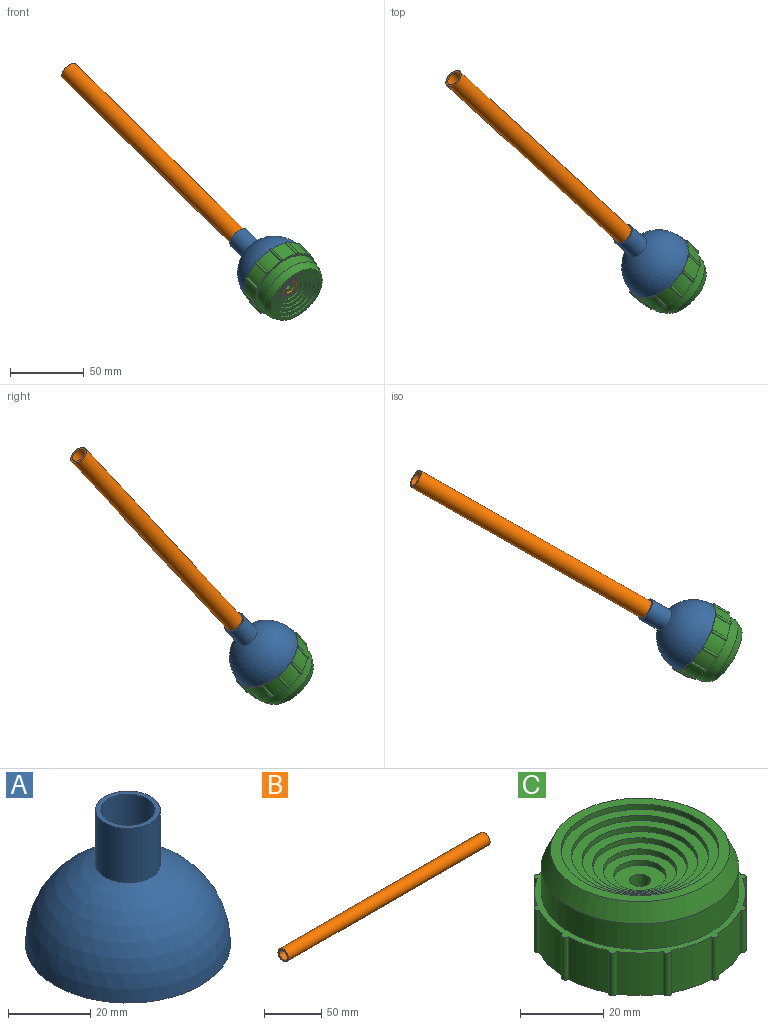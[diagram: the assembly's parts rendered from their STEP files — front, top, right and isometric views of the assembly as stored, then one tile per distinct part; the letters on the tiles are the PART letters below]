
ASSEMBLY  parts=3 mates=4
PART A: 5 faces, bbox 50x50x40 mm
  f0: cylinder r=7.87mm len=16.27mm, axis (0,0,-1), area 805.1mm2, adj f1,f3
  f1: sphere r=25mm, area 3727.1mm2, adj f0,f2
  f2: plane 50x50mm, normal (0,0,-1), area 1826.5mm2, adj f1,f4
  f3: plane 15.75x15.75mm, normal (0,0,1), area 57.8mm2, adj f0,f4
  f4: cylinder r=6.6mm len=40mm, axis (0,0,1), area 1659.8mm2, adj f2,f3
PART B: 4 faces, bbox 250x13x13 mm
  f0: cylinder r=4.92mm len=250mm, axis (-1,0,0), area 7733.1mm2, adj f2,f3
  f1: cylinder r=6.48mm len=250mm, axis (-1,0,0), area 10174mm2, adj f2,f3
  f2: plane 12.95x12.95mm, normal (1,0,0), area 55.7mm2, adj f0,f1
  f3: plane 12.95x12.95mm, normal (-1,0,0), area 55.7mm2, adj f0,f1
PART C: 44 faces, bbox 52.8x52.8x25 mm
  f0: cylinder r=25.4mm len=12.5mm, axis (0,0,1), area 141.2mm2, adj f27,f28,f29,f40
  f1: cylinder r=25.4mm len=12.5mm, axis (0,0,1), area 141.2mm2, adj f27,f28,f39,f40
  f2: cylinder r=25.4mm len=12.5mm, axis (0,0,1), area 141.2mm2, adj f27,f28,f38,f39
  f3: cylinder r=25.4mm len=12.5mm, axis (0,0,1), area 141.2mm2, adj f27,f28,f37,f38
  f4: cylinder r=25.4mm len=12.5mm, axis (0,0,1), area 141.2mm2, adj f27,f28,f36,f37
  f5: cylinder r=25.4mm len=12.5mm, axis (0,0,1), area 141.2mm2, adj f27,f28,f35,f36
  f6: cylinder r=25.4mm len=12.5mm, axis (0,0,1), area 141.2mm2, adj f27,f28,f34,f35
  f7: cylinder r=25.4mm len=12.5mm, axis (0,0,1), area 141.2mm2, adj f27,f28,f33,f34
  f8: cylinder r=25.4mm len=12.5mm, axis (0,0,1), area 141.2mm2, adj f27,f28,f32,f33
  f9: cylinder r=25.4mm len=12.5mm, axis (0,0,1), area 141.2mm2, adj f27,f28,f31,f32
  f10: cylinder r=25.4mm len=12.5mm, axis (0,0,1), area 141.2mm2, adj f27,f28,f30,f31
  f11: cylinder r=25.4mm len=12.5mm, axis (0,0,1), area 141.2mm2, adj f27,f28,f29,f30
  f12: plane 12.7x12.7mm, normal (0,0,1), area 106.4mm2, adj f13,f43
  f13: cylinder r=6.35mm len=12.7mm, axis (0,0,1), area 59.8mm2, adj f12,f14
  f14: plane 17.78x17.78mm, normal (0,0,1), area 121.6mm2, adj f13,f15
  f15: cylinder r=8.89mm len=17.78mm, axis (0,0,1), area 83.8mm2, adj f14,f16
  f16: plane 22.86x22.86mm, normal (0,0,1), area 162.1mm2, adj f15,f17
  f17: cylinder r=11.43mm len=22.86mm, axis (0,0,1), area 107.7mm2, adj f16,f18
  f18: plane 27.94x27.94mm, normal (0,0,1), area 202.7mm2, adj f17,f19
  f19: cylinder r=13.97mm len=27.94mm, axis (0,0,1), area 131.7mm2, adj f18,f20
  f20: plane 33.02x33.02mm, normal (0,0,1), area 243.2mm2, adj f19,f21
  f21: cylinder r=16.51mm len=33.02mm, axis (0,0,1), area 155.6mm2, adj f20,f22
  f22: plane 38.1x38.1mm, normal (0,0,1), area 283.8mm2, adj f21,f23
  f23: cylinder r=19.05mm len=38.1mm, axis (0,0,1), area 179.5mm2, adj f22,f24
  f24: plane 43.18x43.18mm, normal (0,0,1), area 324.3mm2, adj f23,f25
  f25: cone r=23.8mm half-angle=23.8deg, axis (0,0,-1), area 779.5mm2, adj f24,f26
  f26: cylinder r=23.8mm len=47.6mm, axis (0,0,1), area 1121.5mm2, adj f25,f27
  f27: plane 52.8x52.8mm, normal (0,0,1), area 266.3mm2, adj f0,f1,f2,f3,f4,f5,f6,f7
  f28: plane 52.8x52.8mm, normal (0,0,-1), area 1914mm2, adj f0,f1,f2,f3,f4,f5,f6,f7
  f29: cylinder r=1mm len=12.5mm, axis (0,0,-1), area 39.8mm2, adj f0,f11,f27,f28
  f30: cylinder r=1mm len=12.5mm, axis (0,0,-1), area 39.8mm2, adj f10,f11,f27,f28
  f31: cylinder r=1mm len=12.5mm, axis (0,0,-1), area 39.8mm2, adj f9,f10,f27,f28
  f32: cylinder r=1mm len=12.5mm, axis (0,0,-1), area 39.8mm2, adj f8,f9,f27,f28
  f33: cylinder r=1mm len=12.5mm, axis (0,0,-1), area 39.8mm2, adj f7,f8,f27,f28
  f34: cylinder r=1mm len=12.5mm, axis (0,0,-1), area 39.8mm2, adj f6,f7,f27,f28
  f35: cylinder r=1mm len=12.5mm, axis (0,0,-1), area 39.8mm2, adj f5,f6,f27,f28
  f36: cylinder r=1mm len=12.5mm, axis (0,0,-1), area 39.8mm2, adj f4,f5,f27,f28
  f37: cylinder r=1mm len=12.5mm, axis (0,0,-1), area 39.8mm2, adj f3,f4,f27,f28
  f38: cylinder r=1mm len=12.5mm, axis (0,0,-1), area 39.8mm2, adj f2,f3,f27,f28
  f39: cylinder r=1mm len=12.5mm, axis (0,0,-1), area 39.8mm2, adj f1,f2,f27,f28
  f40: cylinder r=1mm len=12.5mm, axis (0,0,-1), area 39.8mm2, adj f0,f1,f27,f28
  f41: cylinder r=6.48mm len=12.95mm, axis (0,0,-1), area 310.1mm2, adj f28,f42
  f42: plane 12.95x12.95mm, normal (0,0,-1), area 111.5mm2, adj f41,f43
  f43: cylinder r=2.54mm len=8.38mm, axis (0,0,1), area 133.7mm2, adj f12,f42
PLACE A rot(axis=(0.31,-0.33,-0.89),173.2deg) t=(3.75,118.7,3.58)mm
PLACE B rot(axis=(-0.52,0.77,-0.36),63.5deg) t=(-135.04,245.82,140.09)mm
PLACE C rot(axis=(-0.06,0.94,-0.35),143.4deg) t=(3.75,118.7,3.58)mm
MATE planar A.f0 <-> C.f28  axis (0.6,-0.55,-0.59) through (3.75,118.7,3.58)mm
MATE slider C.f0 <-> B.f0  axis (-0.6,0.55,0.59) through (3.75,118.7,3.58)mm
MATE slider A.f0 <-> B.f0  axis (0.6,-0.55,-0.59) through (3.75,118.7,3.58)mm
MATE planar B.f0 <-> C.f0  axis (0.6,-0.55,-0.59) through (14.19,109.14,-6.69)mm
